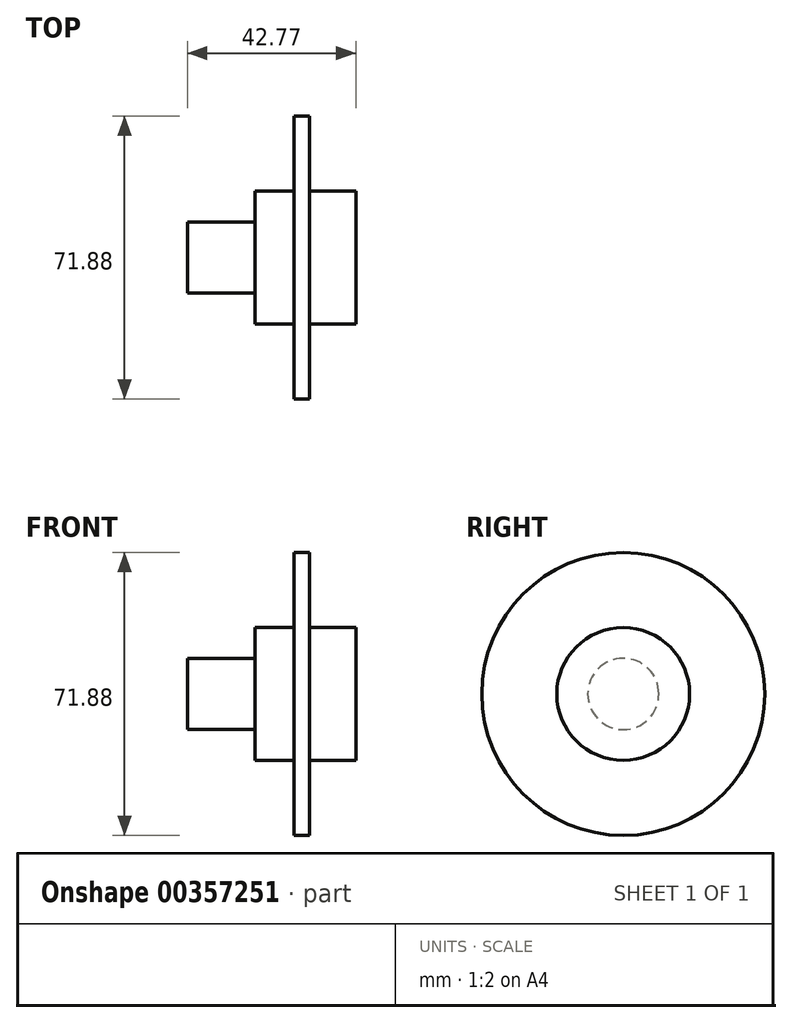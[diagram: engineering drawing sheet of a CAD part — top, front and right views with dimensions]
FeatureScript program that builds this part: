
annotation { "Feature Type Name" : "Feature", "Feature Type Description" : "" }
export const myFeature = defineFeature(function(context is Context, id is Id, definition is map)
    precondition{}
    {
        {
            var Q0;
            Q0=qCreatedBy(makeId("Front.planeOp"),FACE);
            var sketch = newSketch(context, id + "F0", { "sketchPlane" : qUnion([Q0])});
            skLineSegment(sketch, "E0", {"start": v(0, 0) * mm, "end": v(-42.77, 0) * mm});
            skLineSegment(sketch, "E1", {"start": v(-42.77, 0) * mm, "end": v(-42.77, 9.04) * mm});
            skLineSegment(sketch, "E2", {"start": v(-42.77, 9.04) * mm, "end": v(-25.63, 9.04) * mm});
            skLineSegment(sketch, "E3", {"start": v(-25.63, 9.04) * mm, "end": v(-25.63, 16.87) * mm});
            skLineSegment(sketch, "E4", {"start": v(-25.63, 16.87) * mm, "end": v(-15.65, 16.87) * mm});
            skLineSegment(sketch, "E5", {"start": v(-15.65, 16.87) * mm, "end": v(-15.65, 35.94) * mm});
            skLineSegment(sketch, "E6", {"start": v(-15.65, 35.94) * mm, "end": v(-11.73, 35.94) * mm});
            skLineSegment(sketch, "E7", {"start": v(-11.73, 35.94) * mm, "end": v(-11.73, 16.87) * mm});
            skLineSegment(sketch, "E8", {"start": v(-11.73, 16.87) * mm, "end": v(0, 16.87) * mm});
            skLineSegment(sketch, "E9", {"start": v(0, 16.87) * mm, "end": v(0, 0) * mm});
            skSolve(sketch);
        }
        {
            var Q0;
            Q0=makeQuery(id+"F0.imprint","IMPRINT",FACE,{"disambiguationData":[TD([[makeQuery(id+"F0.imprint","IMPRINT",EDGE,{"derivedFrom":sQuery(id+"F0.wireOp",EDGE,"E0")}),-1.0]])]});
            var Q1;
            Q1=sQuery(id+"F0.wireOp",EDGE,"E0");
            revolve(context, id + "F1", {"entities" : qUnion([Q0]), "axis" : qUnion([Q1]), "revolveType" : RevolveType.FULL});
        }
    });
